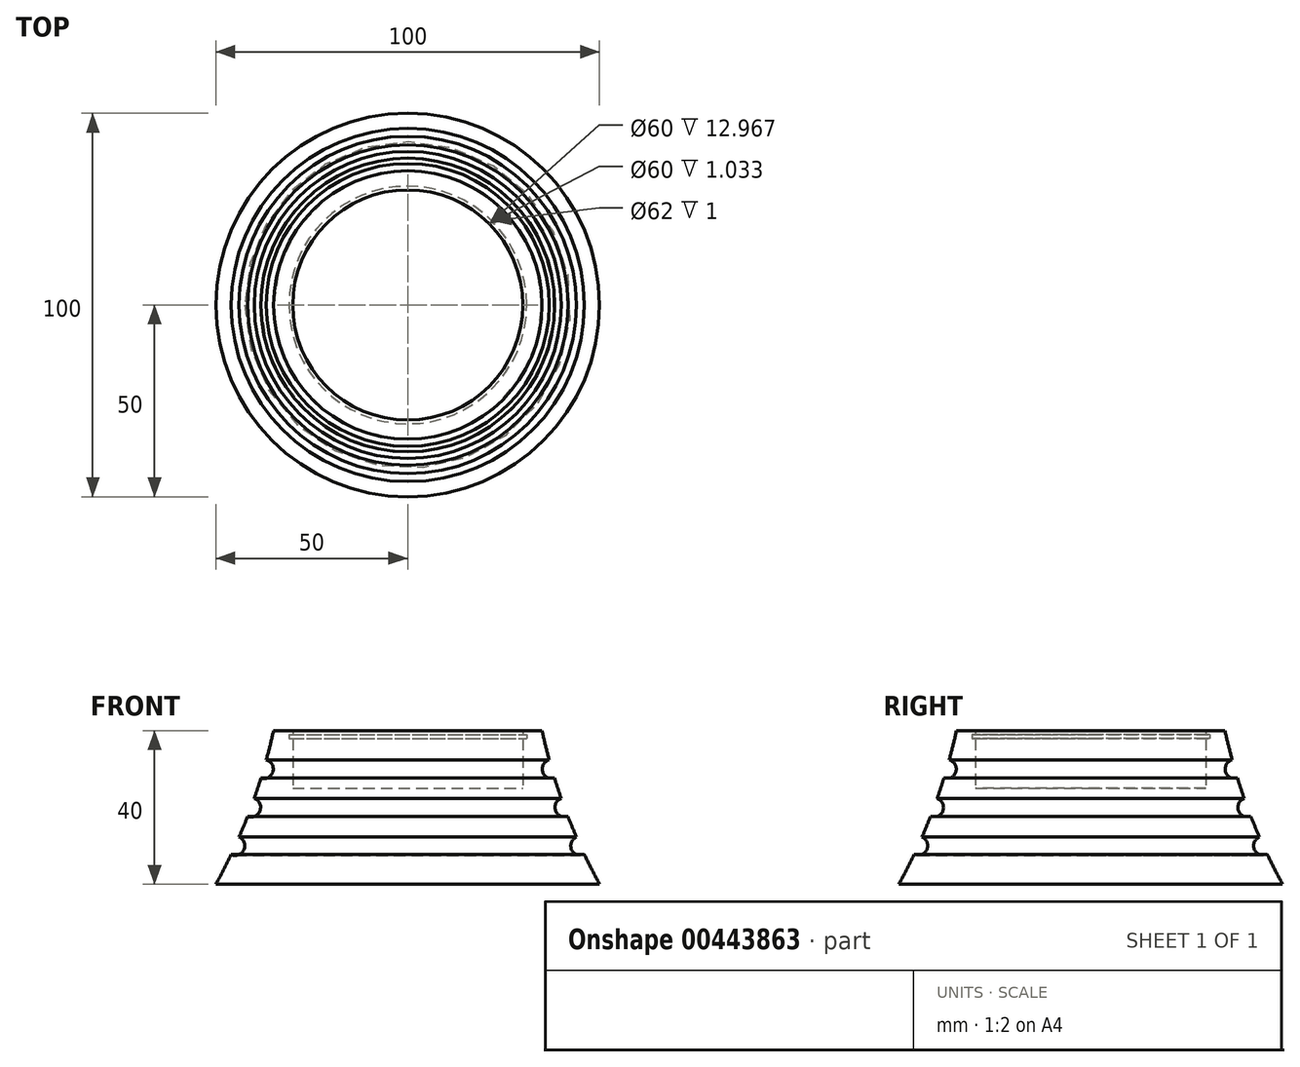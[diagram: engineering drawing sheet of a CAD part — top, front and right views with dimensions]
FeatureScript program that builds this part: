
annotation { "Feature Type Name" : "Feature", "Feature Type Description" : "" }
export const myFeature = defineFeature(function(context is Context, id is Id, definition is map)
    precondition{}
    {
        {
            var Q0;
            Q0=qCreatedBy(makeId("Front.planeOp"),FACE);
            var sketch = newSketch(context, id + "F0", { "sketchPlane" : qUnion([Q0])});
            skLineSegment(sketch, "E0", {"start": v(50, 0) * mm, "end": v(0, 0) * mm});
            skLineSegment(sketch, "E1", {"start": v(0, 0) * mm, "end": v(0, 25) * mm});
            skLineSegment(sketch, "E2", {"start": v(0, 25) * mm, "end": v(30, 25) * mm});
            skLineSegment(sketch, "E3", {"start": v(30, 25) * mm, "end": v(30, 37.97) * mm});
            skLineSegment(sketch, "E4", {"start": v(30, 40) * mm, "end": v(35, 40) * mm});
            skArc(sketch, "E5", {"start": v(35, 40) * mm, "mid": v(35.89, 36.2) * mm, "end": v(36.87, 32.4) * mm});
            skArc(sketch, "E6", {"start": v(36.87, 32.4) * mm, "mid": v(35.16, 29.3) * mm, "end": v(38.28, 27.6) * mm});
            skArc(sketch, "E7", {"start": v(40.02, 22.35) * mm, "mid": v(38.52, 19.13) * mm, "end": v(41.76, 17.66) * mm});
            skArc(sketch, "E8", {"start": v(43.97, 12.28) * mm, "mid": v(42.72, 8.96) * mm, "end": v(46.05, 7.73) * mm});
            skLineSegment(sketch, "E9.bottom", {"start": v(30, 38.97) * mm, "end": v(31, 38.97) * mm});
            skLineSegment(sketch, "E9.top", {"start": v(30, 37.97) * mm, "end": v(31, 37.97) * mm});
            skLineSegment(sketch, "E9.right", {"start": v(31, 38.97) * mm, "end": v(31, 37.97) * mm});
            skLineSegment(sketch, "E10.trimOffspring", {"start": v(30, 38.97) * mm, "end": v(30, 40) * mm});
            skArc(sketch, "E11.trimOffspring", {"start": v(38.28, 27.6) * mm, "mid": v(39.12, 24.97) * mm, "end": v(40.02, 22.35) * mm});
            skArc(sketch, "E12.trimOffspring", {"start": v(41.76, 17.66) * mm, "mid": v(42.84, 14.96) * mm, "end": v(43.97, 12.28) * mm});
            skArc(sketch, "E13.trimOffspring", {"start": v(46.05, 7.73) * mm, "mid": v(47.97, 3.84) * mm, "end": v(50, 0) * mm});
            skSolve(sketch);
        }
        {
            var Q0;
            Q0=makeQuery(id+"F0.imprint","IMPRINT",FACE,{"disambiguationData":[TD([[makeQuery(id+"F0.imprint","IMPRINT",EDGE,{"derivedFrom":sQuery(id+"F0.wireOp",EDGE,"E0")}),-1.0]])]});
            var Q1;
            Q1=sQuery(id+"F0.wireOp",EDGE,"E1");
            revolve(context, id + "F1", {"entities" : qUnion([Q0]), "axis" : qUnion([Q1]), "revolveType" : RevolveType.FULL});
        }
    });
